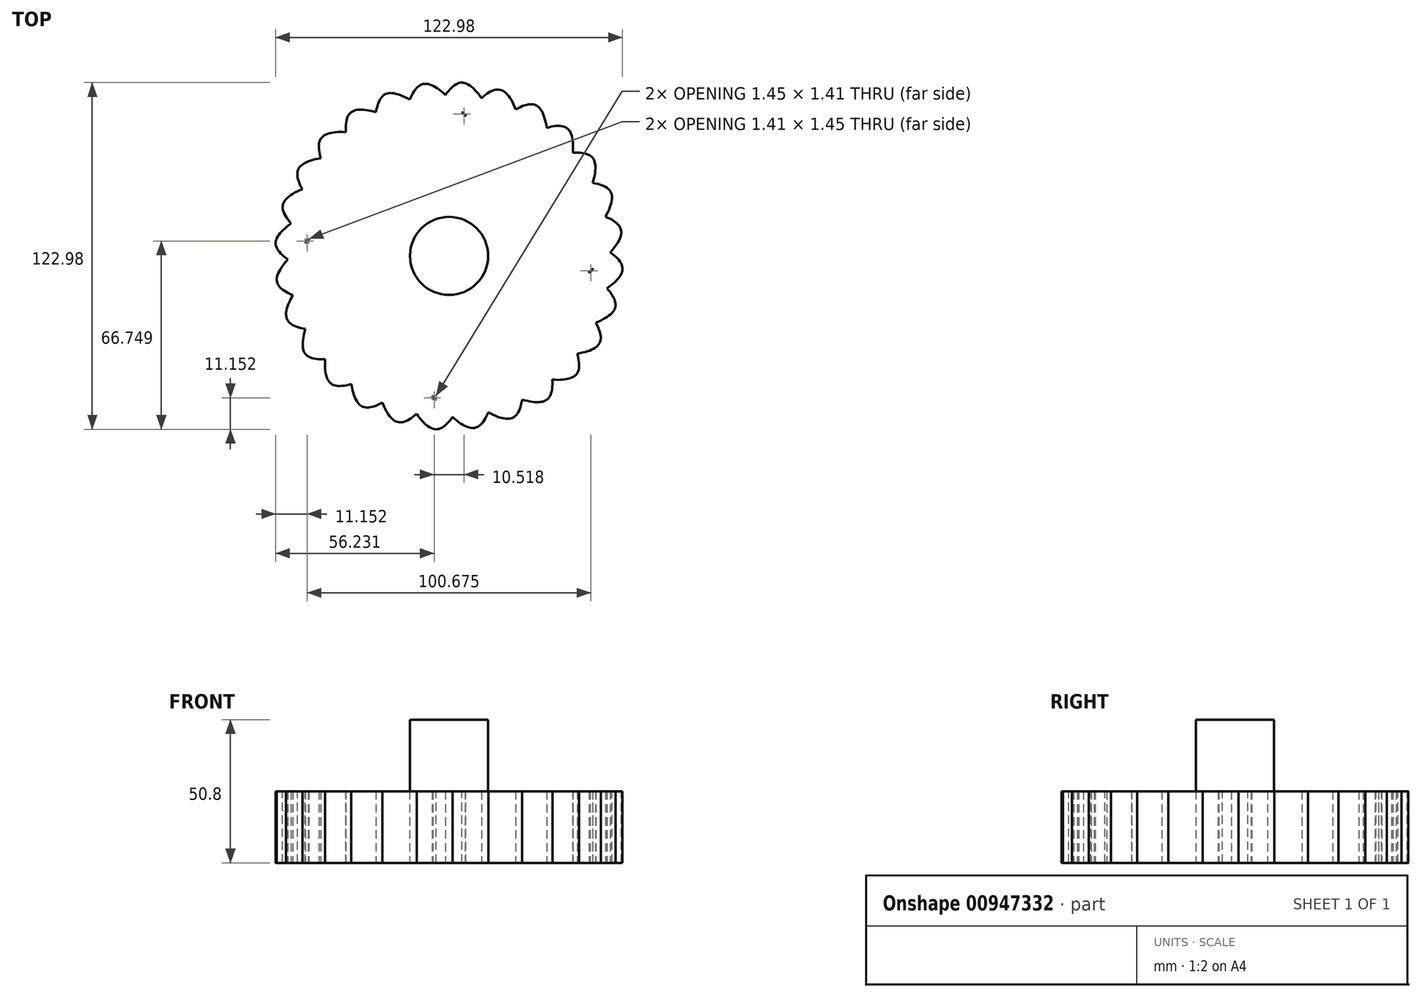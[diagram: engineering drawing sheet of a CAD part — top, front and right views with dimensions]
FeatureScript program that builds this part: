
annotation { "Feature Type Name" : "Feature", "Feature Type Description" : "" }
export const myFeature = defineFeature(function(context is Context, id is Id, definition is map)
    precondition{}
    {
        {
            var Q0;
            Q0=qCreatedBy(makeId("Top.planeOp"),FACE);
            var sketch = newSketch(context, id + "F0", { "sketchPlane" : qUnion([Q0])});
            skCircle(sketch, "E0", {"center": v(0, 0) * mm, "radius": 41.7 * mm});
            skFitSpline(sketch, "E1", {"points": [v(-0.3, 41.7) * mm, v(18.14, 58.93) * mm, v(29.57, 29.41) * mm], "startDerivative": vector(43.22, 58.35) * mm, "endDerivative": vector(17.02, -80.29) * mm});
            skSolve(sketch);
        }
        {
            var Q0;
            Q0 = qSketchRegion(id + "F0", true);
            extrude(context, id + "F1", {"entities" : qUnion([Q0]), "depth" : 25.4 * mm, "offsetDistance" : 25.4 * mm});
        }
        {
            var Q0;
            Q0=makeQuery(id+"F1.opExtrude","SWEPT_BODY",BODY,{"disambiguationData":[OSD([sQuery(id+"F0.wireOp",EDGE,"E0"),sQuery(id+"F0.wireOp",EDGE,"E1")])]});
            var Q1;
            Q1=makeQuery(id+"F1.opExtrude","CAP_EDGE",EDGE,{"disambiguationData":[OSD([sQuery(id+"F0.wireOp",EDGE,"E0")])],"isStart":false});
            circularPattern(context, id + "F2", {"operationType" : NewBodyOperationType.ADD, "entities" : qUnion([Q0]), "axis" : qUnion([Q1]), "angle" : 360 * degree, "instanceCount" : 7, "oppositeDirection" : true, "equalSpace" : true});
        }
        {
            var Q0;
            {var subQ0=makeQuery(id+"F1.opExtrude","SWEPT_FACE",FACE,{"disambiguationData":[OSD([sQuery(id+"F0.wireOp",EDGE,"E0")])]});Q0=makeQuery(id+"F2.boolean.opBoolean","INTERSECT",EDGE,{"disambiguationData":[OD(1.0)],"derivedFrom":[subQ0,makeQuery(id+"F2.opPattern","COPY",FACE,{"derivedFrom":subQ0,"instanceName":"1"}),makeQuery(id+"F2.opPattern","COPY",FACE,{"derivedFrom":subQ0,"instanceName":"2"}),makeQuery(id+"F2.opPattern","COPY",FACE,{"derivedFrom":subQ0,"instanceName":"3"}),makeQuery(id+"F2.opPattern","COPY",FACE,{"derivedFrom":subQ0,"instanceName":"4"}),makeQuery(id+"F2.opPattern","COPY",FACE,{"derivedFrom":subQ0,"instanceName":"5"})]});}
            var Q1;
            {var subQ0=sQuery(id+"F0.wireOp",EDGE,"E1");var subQ1=sQuery(id+"F0.wireOp",EDGE,"E0");Q1=makeQuery(id+"F1.opExtrude","SWEPT_EDGE",EDGE,{"disambiguationData":[OSD([subQ1,subQ0]),TDD([makeQuery(id+"F0.imprint","INTERSECT",VERTEX,{"disambiguationData":[OD(0.0)],"derivedFrom":[subQ1,subQ0]})])]});}
            var Q2;
            {var subQ0=makeQuery(id+"F1.opExtrude","SWEPT_FACE",FACE,{"disambiguationData":[OSD([sQuery(id+"F0.wireOp",EDGE,"E0")])]});Q2=makeQuery(id+"F2.boolean.opBoolean","INTERSECT",EDGE,{"disambiguationData":[OD(0.0)],"derivedFrom":[subQ0,makeQuery(id+"F2.opPattern","COPY",FACE,{"derivedFrom":subQ0,"instanceName":"2"})]});}
            var Q3;
            {var subQ0=sQuery(id+"F0.wireOp",EDGE,"E1");var subQ1=sQuery(id+"F0.wireOp",EDGE,"E0");Q3=makeQuery(id+"F1.opExtrude","SWEPT_EDGE",EDGE,{"disambiguationData":[OSD([subQ1,subQ0]),TDD([makeQuery(id+"F0.imprint","INTERSECT",VERTEX,{"disambiguationData":[OD(1.0)],"derivedFrom":[subQ1,subQ0]})])]});}
            var Q4;
            {var subQ0=makeQuery(id+"F1.opExtrude","SWEPT_FACE",FACE,{"disambiguationData":[OSD([sQuery(id+"F0.wireOp",EDGE,"E0")])]});Q4=makeQuery(id+"F2.boolean.opBoolean","INTERSECT",EDGE,{"disambiguationData":[OD(0.0)],"derivedFrom":[subQ0,makeQuery(id+"F2.opPattern","COPY",FACE,{"derivedFrom":subQ0,"instanceName":"1"}),makeQuery(id+"F2.opPattern","COPY",FACE,{"derivedFrom":subQ0,"instanceName":"2"}),makeQuery(id+"F2.opPattern","COPY",FACE,{"derivedFrom":subQ0,"instanceName":"3"}),makeQuery(id+"F2.opPattern","COPY",FACE,{"derivedFrom":subQ0,"instanceName":"4"}),makeQuery(id+"F2.opPattern","COPY",FACE,{"derivedFrom":subQ0,"instanceName":"5"})]});}
            var Q5;
            {var subQ0=makeQuery(id+"F1.opExtrude","SWEPT_FACE",FACE,{"disambiguationData":[OSD([sQuery(id+"F0.wireOp",EDGE,"E0")])]});Q5=makeQuery(id+"F2.boolean.opBoolean","INTERSECT",EDGE,{"disambiguationData":[OD(1.0)],"derivedFrom":[subQ0,makeQuery(id+"F2.opPattern","COPY",FACE,{"derivedFrom":subQ0,"instanceName":"1"}),makeQuery(id+"F2.opPattern","COPY",FACE,{"derivedFrom":subQ0,"instanceName":"2"}),makeQuery(id+"F2.opPattern","COPY",FACE,{"derivedFrom":subQ0,"instanceName":"3"}),makeQuery(id+"F2.opPattern","COPY",FACE,{"derivedFrom":subQ0,"instanceName":"4"}),makeQuery(id+"F2.opPattern","COPY",FACE,{"derivedFrom":subQ0,"instanceName":"6"})]});}
            var Q6;
            {var subQ0=makeQuery(id+"F1.opExtrude","SWEPT_FACE",FACE,{"disambiguationData":[OSD([sQuery(id+"F0.wireOp",EDGE,"E0")])]});Q6=makeQuery(id+"F2.boolean.opBoolean","INTERSECT",EDGE,{"disambiguationData":[OD(0.0)],"derivedFrom":[subQ0,makeQuery(id+"F2.opPattern","COPY",FACE,{"derivedFrom":subQ0,"instanceName":"1"}),makeQuery(id+"F2.opPattern","COPY",FACE,{"derivedFrom":subQ0,"instanceName":"2"}),makeQuery(id+"F2.opPattern","COPY",FACE,{"derivedFrom":subQ0,"instanceName":"3"}),makeQuery(id+"F2.opPattern","COPY",FACE,{"derivedFrom":subQ0,"instanceName":"4"}),makeQuery(id+"F2.opPattern","COPY",FACE,{"derivedFrom":subQ0,"instanceName":"6"})]});}
            var Q7;
            {var subQ0=makeQuery(id+"F1.opExtrude","SWEPT_FACE",FACE,{"disambiguationData":[OSD([sQuery(id+"F0.wireOp",EDGE,"E0")])]});Q7=makeQuery(id+"F2.boolean.opBoolean","INTERSECT",EDGE,{"disambiguationData":[OD(1.0)],"derivedFrom":[subQ0,makeQuery(id+"F2.opPattern","COPY",FACE,{"derivedFrom":subQ0,"instanceName":"1"}),makeQuery(id+"F2.opPattern","COPY",FACE,{"derivedFrom":subQ0,"instanceName":"2"}),makeQuery(id+"F2.opPattern","COPY",FACE,{"derivedFrom":subQ0,"instanceName":"3"}),makeQuery(id+"F2.opPattern","COPY",FACE,{"derivedFrom":subQ0,"instanceName":"5"})]});}
            var Q8;
            {var subQ0=makeQuery(id+"F1.opExtrude","SWEPT_FACE",FACE,{"disambiguationData":[OSD([sQuery(id+"F0.wireOp",EDGE,"E0")])]});Q8=makeQuery(id+"F2.boolean.opBoolean","INTERSECT",EDGE,{"disambiguationData":[OD(0.0)],"derivedFrom":[subQ0,makeQuery(id+"F2.opPattern","COPY",FACE,{"derivedFrom":subQ0,"instanceName":"1"}),makeQuery(id+"F2.opPattern","COPY",FACE,{"derivedFrom":subQ0,"instanceName":"2"}),makeQuery(id+"F2.opPattern","COPY",FACE,{"derivedFrom":subQ0,"instanceName":"3"}),makeQuery(id+"F2.opPattern","COPY",FACE,{"derivedFrom":subQ0,"instanceName":"5"})]});}
            var Q9;
            {var subQ0=makeQuery(id+"F1.opExtrude","SWEPT_FACE",FACE,{"disambiguationData":[OSD([sQuery(id+"F0.wireOp",EDGE,"E0")])]});Q9=makeQuery(id+"F2.boolean.opBoolean","INTERSECT",EDGE,{"disambiguationData":[OD(1.0)],"derivedFrom":[subQ0,makeQuery(id+"F2.opPattern","COPY",FACE,{"derivedFrom":subQ0,"instanceName":"1"}),makeQuery(id+"F2.opPattern","COPY",FACE,{"derivedFrom":subQ0,"instanceName":"2"}),makeQuery(id+"F2.opPattern","COPY",FACE,{"derivedFrom":subQ0,"instanceName":"4"})]});}
            var Q10;
            {var subQ0=makeQuery(id+"F1.opExtrude","SWEPT_FACE",FACE,{"disambiguationData":[OSD([sQuery(id+"F0.wireOp",EDGE,"E0")])]});Q10=makeQuery(id+"F2.boolean.opBoolean","INTERSECT",EDGE,{"disambiguationData":[OD(1.0)],"derivedFrom":[subQ0,makeQuery(id+"F2.opPattern","COPY",FACE,{"derivedFrom":subQ0,"instanceName":"1"}),makeQuery(id+"F2.opPattern","COPY",FACE,{"derivedFrom":subQ0,"instanceName":"3"})]});}
            var Q11;
            {var subQ0=makeQuery(id+"F1.opExtrude","SWEPT_FACE",FACE,{"disambiguationData":[OSD([sQuery(id+"F0.wireOp",EDGE,"E0")])]});Q11=makeQuery(id+"F2.boolean.opBoolean","INTERSECT",EDGE,{"disambiguationData":[OD(0.0)],"derivedFrom":[subQ0,makeQuery(id+"F2.opPattern","COPY",FACE,{"derivedFrom":subQ0,"instanceName":"1"}),makeQuery(id+"F2.opPattern","COPY",FACE,{"derivedFrom":subQ0,"instanceName":"2"}),makeQuery(id+"F2.opPattern","COPY",FACE,{"derivedFrom":subQ0,"instanceName":"4"})]});}
            var Q12;
            {var subQ0=makeQuery(id+"F1.opExtrude","SWEPT_FACE",FACE,{"disambiguationData":[OSD([sQuery(id+"F0.wireOp",EDGE,"E0")])]});Q12=makeQuery(id+"F2.boolean.opBoolean","INTERSECT",EDGE,{"disambiguationData":[OD(1.0)],"derivedFrom":[subQ0,makeQuery(id+"F2.opPattern","COPY",FACE,{"derivedFrom":subQ0,"instanceName":"2"})]});}
            var Q13;
            {var subQ0=makeQuery(id+"F1.opExtrude","SWEPT_FACE",FACE,{"disambiguationData":[OSD([sQuery(id+"F0.wireOp",EDGE,"E0")])]});Q13=makeQuery(id+"F2.boolean.opBoolean","INTERSECT",EDGE,{"disambiguationData":[OD(0.0)],"derivedFrom":[subQ0,makeQuery(id+"F2.opPattern","COPY",FACE,{"derivedFrom":subQ0,"instanceName":"1"}),makeQuery(id+"F2.opPattern","COPY",FACE,{"derivedFrom":subQ0,"instanceName":"3"})]});}
            fillet(context, id + "F3", {"entities" : qUnion([Q0, Q1, Q2, Q3, Q4, Q5, Q6, Q7, Q8, Q9, Q10, Q11, Q12, Q13]), "radius" : 5.08 * mm, "tangentPropagation" : true, "allowEdgeOverflow" : false});
        }
        {
            var Q0;
            {var subQ0=makeQuery(id+"F1.opExtrude","CAP_FACE",FACE,{"disambiguationData":[OSD([sQuery(id+"F0.wireOp",EDGE,"E0"),sQuery(id+"F0.wireOp",EDGE,"E1")])],"isStart":false});Q0=makeQuery(id+"F2.boolean.opBoolean","MERGE",FACE,{"derivedFrom":[subQ0,makeQuery(id+"F2.opPattern","COPY",FACE,{"derivedFrom":subQ0,"instanceName":"1"}),makeQuery(id+"F2.opPattern","COPY",FACE,{"derivedFrom":subQ0,"instanceName":"2"}),makeQuery(id+"F2.opPattern","COPY",FACE,{"derivedFrom":subQ0,"instanceName":"3"}),makeQuery(id+"F2.opPattern","COPY",FACE,{"derivedFrom":subQ0,"instanceName":"4"}),makeQuery(id+"F2.opPattern","COPY",FACE,{"derivedFrom":subQ0,"instanceName":"5"}),makeQuery(id+"F2.opPattern","COPY",FACE,{"derivedFrom":subQ0,"instanceName":"6"})]});}
            var sketch = newSketch(context, id + "F4", { "sketchPlane" : qUnion([Q0])});
            skFitSpline(sketch, "E2", {"points": [v(-36.39, -6.71) * mm, v(-51.9, 1.89) * mm, v(-35.13, 10.07) * mm, v(-36.39, -6.71) * mm]});
            skSolve(sketch);
        }
        {
            var Q0;
            Q0 = qSketchRegion(id + "F4", true);
            extrude(context, id + "F5", {"entities" : qUnion([Q0]), "operationType" : NewBodyOperationType.REMOVE, "oppositeDirection" : true, "depth" : 25.4 * mm, "offsetDistance" : 25.4 * mm});
        }
        {
            var Q0;
            {var subQ0=makeQuery(id+"F1.opExtrude","CAP_FACE",FACE,{"disambiguationData":[OSD([sQuery(id+"F0.wireOp",EDGE,"E0"),sQuery(id+"F0.wireOp",EDGE,"E1")])],"isStart":false});Q0=makeQuery(id+"F2.boolean.opBoolean","MERGE",FACE,{"derivedFrom":[subQ0,makeQuery(id+"F2.opPattern","COPY",FACE,{"derivedFrom":subQ0,"instanceName":"1"}),makeQuery(id+"F2.opPattern","COPY",FACE,{"derivedFrom":subQ0,"instanceName":"2"}),makeQuery(id+"F2.opPattern","COPY",FACE,{"derivedFrom":subQ0,"instanceName":"3"}),makeQuery(id+"F2.opPattern","COPY",FACE,{"derivedFrom":subQ0,"instanceName":"4"}),makeQuery(id+"F2.opPattern","COPY",FACE,{"derivedFrom":subQ0,"instanceName":"5"}),makeQuery(id+"F2.opPattern","COPY",FACE,{"derivedFrom":subQ0,"instanceName":"6"})]});}
            var sketch = newSketch(context, id + "F6", { "sketchPlane" : qUnion([Q0])});
            skCircle(sketch, "E3", {"center": v(0, 0) * mm, "radius": 13.84 * mm});
            skSolve(sketch);
        }
        {
            var Q0;
            Q0 = qSketchRegion(id + "F6", true);
            extrude(context, id + "F7", {"entities" : qUnion([Q0]), "operationType" : NewBodyOperationType.ADD, "depth" : 25.4 * mm, "offsetDistance" : 25.4 * mm});
        }
        {
            var Q0;
            Q0=makeQuery(id+"F1.opExtrude","SWEPT_BODY",BODY,{"disambiguationData":[OSD([sQuery(id+"F0.wireOp",EDGE,"E0"),sQuery(id+"F0.wireOp",EDGE,"E1")])]});
            var Q1;
            Q1=makeQuery(id+"F7.opExtrude","CAP_EDGE",EDGE,{"disambiguationData":[OSD([sQuery(id+"F6.wireOp",EDGE,"E3")])],"isStart":false});
            circularPattern(context, id + "F8", {"operationType" : NewBodyOperationType.ADD, "entities" : qUnion([Q0]), "axis" : qUnion([Q1]), "angle" : 360 * degree, "instanceCount" : 4, "equalSpace" : true});
        }
    });
